# Revit family: Specialty_Equipment-Metal_Raceway-Hubbell_Wiring-4_Gang_Two_Style_Line_Two_Blank-HBL47472RRXX
name_source: partatom
category: Specialty Equipment
revit_build: Autodesk Revit 2015 (Build: 20140606_1530(x64)
units: mm (PartAtom-declared; Revit-internal decimal feet)

## types (2) — shared parameters
Assembly Code = D5090900
Default Elevation = 0' - 0"
Description = 4-Gang Cover, Two Style Line Openings, Two Blank
Host Note = Add in Plan View; Host to Wall
Manufacturer = Hubbell-Wiring
Product Documentation Link = http://www.hubbell-wiring.com
Product Page URL = http://ecatalog.hubbell-wiring.com
Product data url = https://bimobject.com
URL = http://www.hubbell-wiring.com

## per-type parameters (varying)
| type | Cable Tray Material | Model |
| HBL47472RRXXGY - Gray | Metal-Hubbell-Gray Powder Coat | HBL47472RRXXGY |
| HBL47472RRXXIV - Ivory | Metal-Hubbell-Ivory Powder Coat | HBL47472RRXXIV |

## geometry (parser evidence)
native form markers: Blend x33, Sweep x1
no freeform markers — native parametric forms only
